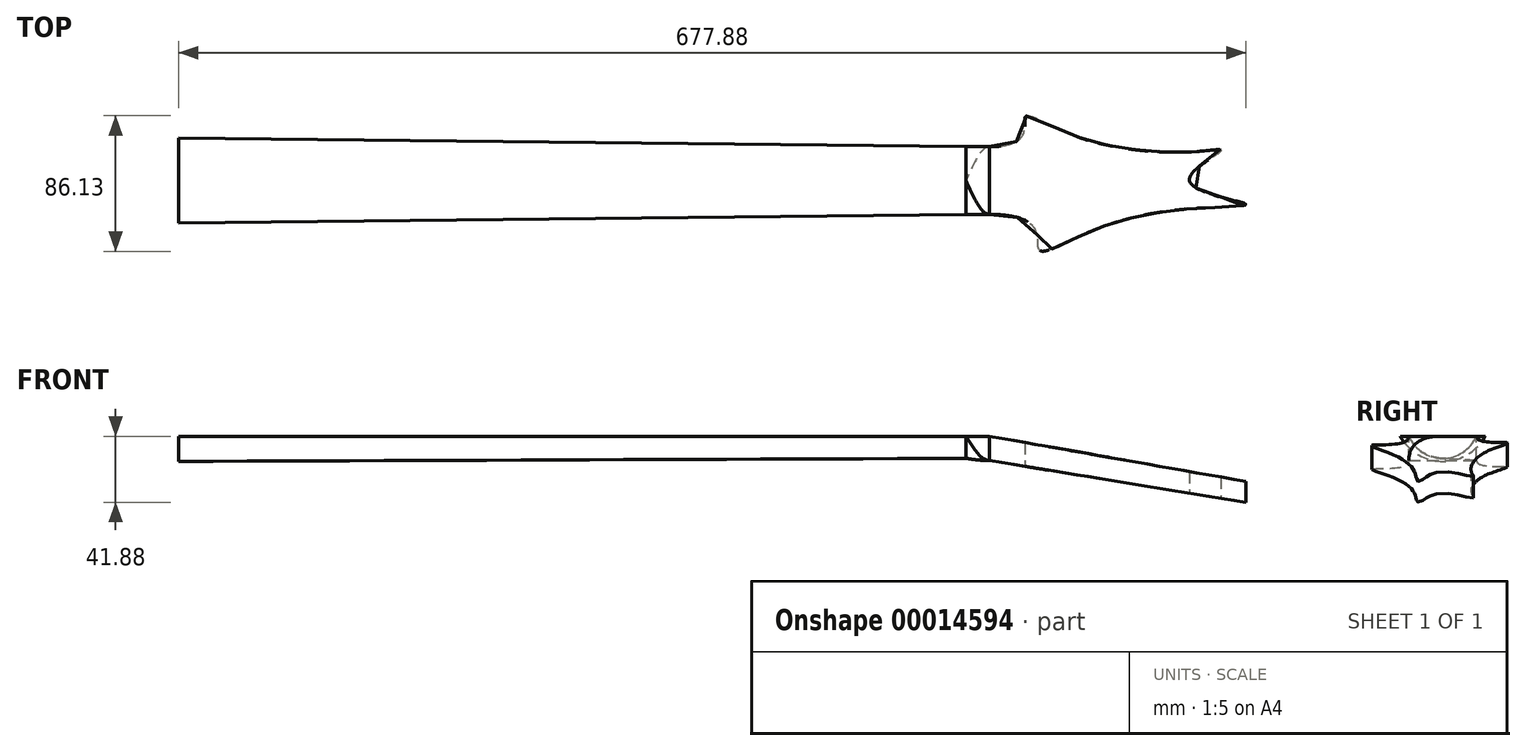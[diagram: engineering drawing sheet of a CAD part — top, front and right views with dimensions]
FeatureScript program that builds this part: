
annotation { "Feature Type Name" : "Feature", "Feature Type Description" : "" }
export const myFeature = defineFeature(function(context is Context, id is Id, definition is map)
    precondition{}
    {
        {
            var Q0;
            Q0=qCreatedBy(makeId("Top.planeOp"),FACE);
            var sketch = newSketch(context, id + "F0", { "sketchPlane" : qUnion([Q0])});
            skLineSegment(sketch, "E0", {"start": v(-427.88, 0) * mm, "end": v(673.93, 0) * mm, "construction": true});
            skLineSegment(sketch, "E1", {"start": v(147.7, 0) * mm, "end": v(147.7, 27) * mm});
            skLineSegment(sketch, "E2", {"start": v(147.7, 27) * mm, "end": v(647.7, 21.5) * mm});
            skLineSegment(sketch, "E3", {"start": v(647.7, 21.5) * mm, "end": v(647.7, 0) * mm});
            skLineSegment(sketch, "E4.0.MirrorCS", {"start": v(147.7, 0) * mm, "end": v(147.7, -27) * mm});
            skLineSegment(sketch, "E5.0.MirrorCS", {"start": v(147.7, -27) * mm, "end": v(647.7, -21.5) * mm});
            skLineSegment(sketch, "E6.0.MirrorCS", {"start": v(647.7, -21.5) * mm, "end": v(647.7, 0) * mm});
            skSolve(sketch);
        }
        {
            var Q0;
            Q0=qCreatedBy(makeId("Right.planeOp"),FACE);
            cPlane(context, id + "F1", {"entities" : qUnion([Q0]), "cplaneType" : CPlaneType.OFFSET, "offset" : 647.7 * mm, "width" : 150 * mm, "height" : 150 * mm});
        }
        {
            var Q0;
            Q0=qCreatedBy(id+"F1.planeOp",FACE);
            cPlane(context, id + "F2", {"entities" : qUnion([Q0]), "cplaneType" : CPlaneType.OFFSET, "offset" : 500 * mm, "oppositeDirection" : true, "width" : 150 * mm, "height" : 150 * mm});
        }
        {
            var Q0;
            Q0=qCreatedBy(id+"F2.planeOp",FACE);
            var sketch = newSketch(context, id + "F3", { "sketchPlane" : qUnion([Q0])});
            skPoint(sketch, "E7.0", {"position": v(-27, 0) * mm});
            skPoint(sketch, "E7.1", {"position": v(27, 0) * mm});
            skLineSegment(sketch, "E8", {"start": v(-27, 0) * mm, "end": v(27, 0) * mm});
            skArc(sketch, "E9", {"start": v(-27, 0) * mm, "mid": v(0, -16) * mm, "end": v(27, 0) * mm});
            skSolve(sketch);
        }
        {
            var Q0;
            Q0=qCreatedBy(id+"F1.planeOp",FACE);
            var sketch = newSketch(context, id + "F4", { "sketchPlane" : qUnion([Q0])});
            skPoint(sketch, "E10.0", {"position": v(-21.5, 0) * mm});
            skPoint(sketch, "E10.1", {"position": v(21.5, 0) * mm});
            skLineSegment(sketch, "E11", {"start": v(-21.5, 0) * mm, "end": v(21.5, 0) * mm});
            skArc(sketch, "E12", {"start": v(-21.5, 0) * mm, "mid": v(0, -14) * mm, "end": v(21.5, 0) * mm});
            skSolve(sketch);
        }
        {
            var Q0;
            Q0=qCreatedBy(makeId("Top.planeOp"),FACE);
            var sketch = newSketch(context, id + "F5", { "sketchPlane" : qUnion([Q0])});
            skLineSegment(sketch, "E13", {"start": v(662.7, -30.67) * mm, "end": v(662.7, 43.76) * mm, "construction": true});
            skPoint(sketch, "E14", {"position": v(662.7, 21.5) * mm});
            skPoint(sketch, "E15", {"position": v(662.7, -21.5) * mm});
            skFitSpline(sketch, "E16", {"points": [v(662.7, 21.5) * mm, v(685.37, 40.35) * mm, v(714.05, 29.38) * mm, v(793.63, 18.4) * mm, v(809.55, 18.56) * mm, v(789.66, 0) * mm, v(825.15, -14.76) * mm, v(791.27, -17.8) * mm, v(723.14, -33.88) * mm, v(694.15, -43.97) * mm, v(662.7, -21.5) * mm], "startDerivative": vector(968.82, 0) * mm, "endDerivative": vector(-1140.74, 0) * mm});
            skLineSegment(sketch, "E17", {"start": v(662.7, -21.5) * mm, "end": v(662.7, 21.5) * mm});
            skSolve(sketch);
        }
        {
            var Q0;
            Q0=makeQuery(id+"F5.imprint","IMPRINT",FACE,{"disambiguationData":[TD([[makeQuery(id+"F5.imprint","IMPRINT",EDGE,{"derivedFrom":sQuery(id+"F5.wireOp",EDGE,"E16")}),-1.0]])]});
            extrude(context, id + "F6", {"entities" : qUnion([Q0]), "oppositeDirection" : true, "depth" : 50 * mm});
        }
        {
            var Q0;
            Q0=qCreatedBy(makeId("Front.planeOp"),FACE);
            var sketch = newSketch(context, id + "F7", { "sketchPlane" : qUnion([Q0])});
            skPoint(sketch, "E18.0", {"position": v(662.7, 0) * mm});
            skLineSegment(sketch, "E19", {"start": v(662.7, 0) * mm, "end": v(836.7, -30.68) * mm});
            skLineSegment(sketch, "E20", {"start": v(836.7, -30.68) * mm, "end": v(836.7, 27.2) * mm});
            skLineSegment(sketch, "E21", {"start": v(836.7, 27.2) * mm, "end": v(656.4, 27.2) * mm});
            skLineSegment(sketch, "E22", {"start": v(656.4, 27.2) * mm, "end": v(662.7, 0) * mm});
            skLineSegment(sketch, "E23", {"start": v(659.68, -15) * mm, "end": v(836.7, -43.68) * mm});
            skLineSegment(sketch, "E24", {"start": v(836.7, -43.68) * mm, "end": v(836.7, -62.76) * mm});
            skLineSegment(sketch, "E25", {"start": v(836.7, -62.76) * mm, "end": v(649.6, -59.83) * mm});
            skLineSegment(sketch, "E26", {"start": v(649.6, -59.83) * mm, "end": v(659.68, -15) * mm});
            skPoint(sketch, "E27.0", {"position": v(647.7, 0) * mm});
            skSolve(sketch);
        }
        {
            var Q0;
            Q0=makeQuery(id+"F7.imprint","IMPRINT",FACE,{"disambiguationData":[TD([[makeQuery(id+"F7.imprint","IMPRINT",EDGE,{"derivedFrom":sQuery(id+"F7.wireOp",EDGE,"E19")}),1.0]])]});
            var Q1;
            Q1=makeQuery(id+"F7.imprint","IMPRINT",FACE,{"disambiguationData":[TD([[makeQuery(id+"F7.imprint","IMPRINT",EDGE,{"derivedFrom":sQuery(id+"F7.wireOp",EDGE,"E23")}),-1.0]])]});
            extrude(context, id + "F8", {"entities" : qUnion([Q0, Q1]), "operationType" : NewBodyOperationType.REMOVE, "endBound" : BoundingType.SYMMETRIC, "oppositeDirection" : true, "depth" : 120 * mm});
        }
        {
            var Q1;
            Q1=makeQuery(id+"F4.imprint","IMPRINT",FACE,{"disambiguationData":[TD([[makeQuery(id+"F4.imprint","IMPRINT",EDGE,{"derivedFrom":sQuery(id+"F4.wireOp",EDGE,"E11")}),-1.0]])]});
            var Q2;
            Q2=makeQuery(id+"F3.imprint","IMPRINT",FACE,{"disambiguationData":[TD([[makeQuery(id+"F3.imprint","IMPRINT",EDGE,{"derivedFrom":sQuery(id+"F3.wireOp",EDGE,"E8")}),-1.0]])]});
            loft(context, id + "F9", {"operationType" : NewBodyOperationType.ADD, "sheetProfilesArray" : [{ "sheetProfileEntities" : qUnion([Q1]) }, { "sheetProfileEntities" : qUnion([Q2]) }]});
        }
        {
            var Q0;
            Q0=qCreatedBy(makeId("Top.planeOp"),FACE);
            var sketch = newSketch(context, id + "F10", { "sketchPlane" : qUnion([Q0])});
            skPoint(sketch, "E28.0", {"position": v(647.7, 21.5) * mm});
            skPoint(sketch, "E28.1", {"position": v(662.7, 21.5) * mm});
            skPoint(sketch, "E28.2", {"position": v(662.7, -21.5) * mm});
            skPoint(sketch, "E28.3", {"position": v(647.7, -21.5) * mm});
            skLineSegment(sketch, "E29", {"start": v(647.7, 21.5) * mm, "end": v(647.7, -21.5) * mm});
            skLineSegment(sketch, "E30", {"start": v(647.7, -21.5) * mm, "end": v(662.7, -21.5) * mm});
            skLineSegment(sketch, "E31", {"start": v(662.7, -21.5) * mm, "end": v(662.7, 21.5) * mm});
            skLineSegment(sketch, "E32", {"start": v(662.7, 21.5) * mm, "end": v(647.7, 21.5) * mm});
            skSolve(sketch);
        }
        {
            var Q0;
            Q0=makeQuery(id+"F6.opExtrude","SWEPT_FACE",FACE,{"disambiguationData":[OSD([sQuery(id+"F5.wireOp",EDGE,"E17")])]});
            var Q1;
            Q1=makeQuery(id+"F4.imprint","IMPRINT",FACE,{"disambiguationData":[TD([[makeQuery(id+"F4.imprint","IMPRINT",EDGE,{"derivedFrom":sQuery(id+"F4.wireOp",EDGE,"E11")}),-1.0]])]});
            var Q2;
            Q2=sQuery(id+"F4.wireOp",VERTEX,"E10.0");
            var Q3;
            Q3=sQuery(id+"F10.wireOp",VERTEX,"E28.2");
            loft(context, id + "F11", {"startCondition" : LoftEndDerivativeType.NORMAL_TO_PROFILE, "startMagnitude" : 1, "sheetProfilesArray" : [{ "sheetProfileEntities" : qUnion([Q0]) }, { "sheetProfileEntities" : qUnion([Q1]) }], "connections" : [{ "connectionEntities" : qUnion([Q2, Q3]), "connectionEdgeQueries" : qUnion([]), "connectionEdgeParameters" : [] }]});
        }
    });
